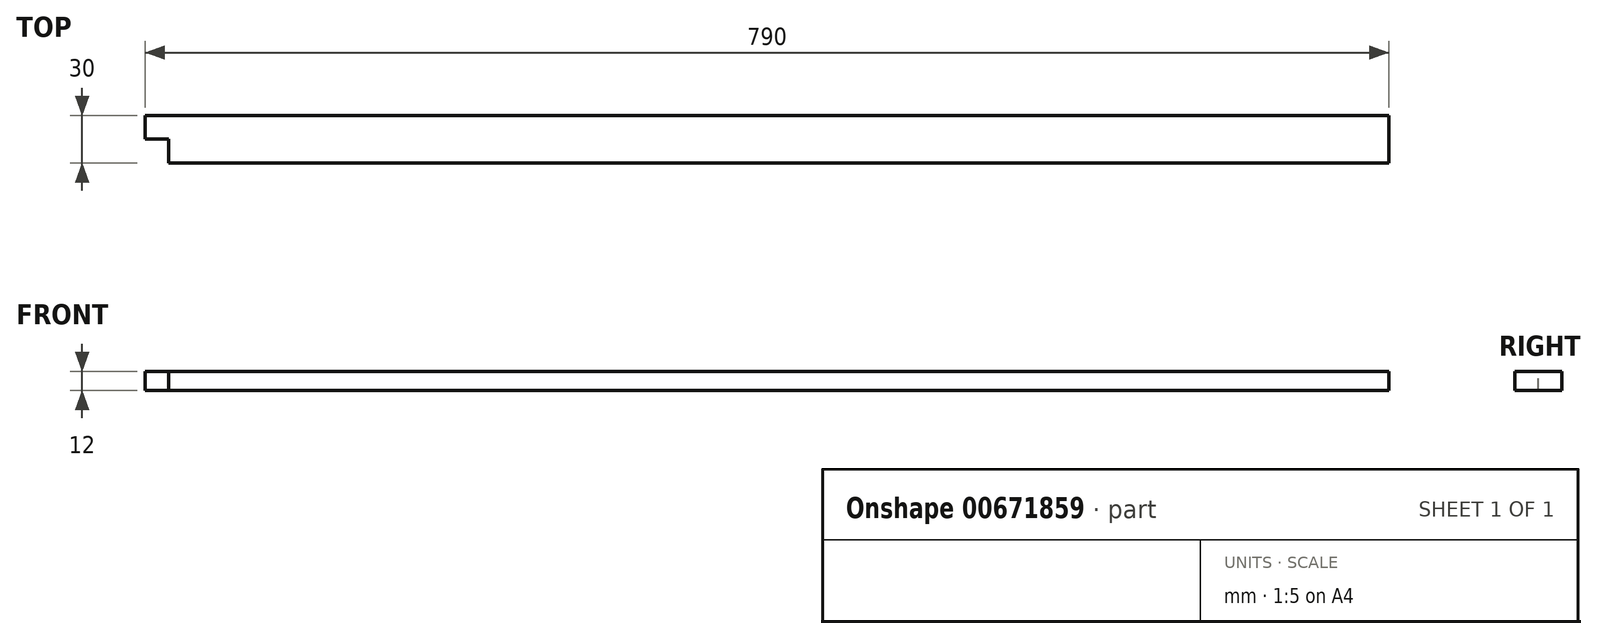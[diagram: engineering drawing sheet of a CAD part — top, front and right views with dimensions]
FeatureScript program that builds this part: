
annotation { "Feature Type Name" : "Feature", "Feature Type Description" : "" }
export const myFeature = defineFeature(function(context is Context, id is Id, definition is map)
    precondition{}
    {
        {
            var Q0;
            Q0=qCreatedBy(makeId("Top.planeOp"),FACE);
            var sketch = newSketch(context, id + "F0", { "sketchPlane" : qUnion([Q0])});
            skLineSegment(sketch, "E0.bottom", {"start": v(-395, -15) * mm, "end": v(395, -15) * mm});
            skLineSegment(sketch, "E0.top", {"start": v(-395, 15) * mm, "end": v(395, 15) * mm});
            skLineSegment(sketch, "E0.left", {"start": v(-395, -15) * mm, "end": v(-395, 15) * mm});
            skLineSegment(sketch, "E0.right", {"start": v(395, -15) * mm, "end": v(395, 15) * mm});
            skPoint(sketch, "E0.middle", {"position": v(0, 0) * mm});
            skSolve(sketch);
        }
        {
            var Q0;
            Q0=makeQuery(id+"F0.imprint","IMPRINT",FACE,{"disambiguationData":[TD([[makeQuery(id+"F0.imprint","IMPRINT",EDGE,{"derivedFrom":sQuery(id+"F0.wireOp",EDGE,"E0.bottom")}),1.0]])]});
            extrude(context, id + "F1", {"entities" : qUnion([Q0]), "depth" : 12 * mm, "offsetDistance" : 25 * mm});
        }
        {
            var Q0;
            Q0=makeQuery(id+"F1.opExtrude","CAP_FACE",FACE,{"disambiguationData":[OSD([sQuery(id+"F0.wireOp",EDGE,"E0.bottom"),sQuery(id+"F0.wireOp",EDGE,"E0.top"),sQuery(id+"F0.wireOp",EDGE,"E0.left"),sQuery(id+"F0.wireOp",EDGE,"E0.right")])],"isStart":false});
            var sketch = newSketch(context, id + "F2", { "sketchPlane" : qUnion([Q0])});
            skLineSegment(sketch, "E1", {"start": v(-395, 0) * mm, "end": v(-380, 0) * mm});
            skLineSegment(sketch, "E2", {"start": v(-380, 0) * mm, "end": v(-380, -15) * mm});
            skSolve(sketch);
        }
        {
            var Q0;
            {var subQ0=sQuery(id+"F2.wireOp",EDGE,"E1");Q0=makeQuery(id+"F2.imprint","IMPRINT",FACE,{"disambiguationData":[TD([[makeQuery(id+"F2.imprint","IMPRINT",EDGE,{"derivedFrom":subQ0}),-1.0]])]});}
            extrude(context, id + "F3", {"entities" : qUnion([Q0]), "operationType" : NewBodyOperationType.REMOVE, "endBound" : BoundingType.THROUGH_ALL, "oppositeDirection" : true, "depth" : 25 * mm, "offsetDistance" : 25 * mm});
        }
    });
